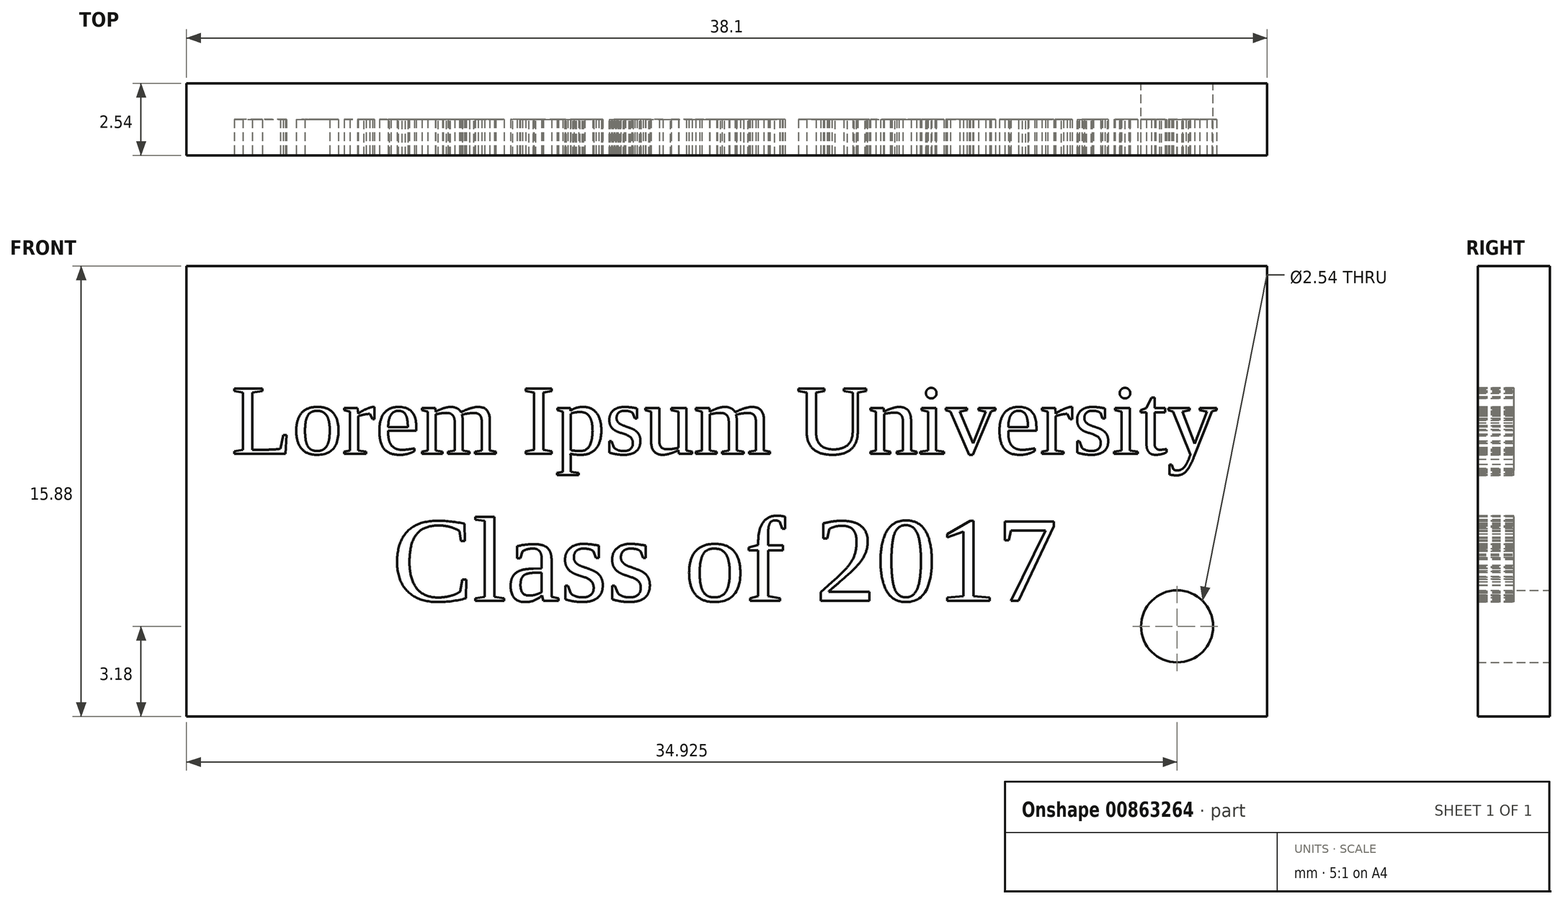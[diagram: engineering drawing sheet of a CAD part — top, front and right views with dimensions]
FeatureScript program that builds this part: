
annotation { "Feature Type Name" : "Feature", "Feature Type Description" : "" }
export const myFeature = defineFeature(function(context is Context, id is Id, definition is map)
    precondition{}
    {
        {
            var Q0;
            Q0=qCreatedBy(makeId("Front.planeOp"),FACE);
            var sketch = newSketch(context, id + "F0", { "sketchPlane" : qUnion([Q0])});
            skLineSegment(sketch, "E0.bottom", {"start": v(0, 0) * mm, "end": v(38.1, 0) * mm});
            skLineSegment(sketch, "E0.top", {"start": v(0, -15.88) * mm, "end": v(38.1, -15.88) * mm});
            skLineSegment(sketch, "E0.left", {"start": v(0, 0) * mm, "end": v(0, -15.88) * mm});
            skLineSegment(sketch, "E0.right", {"start": v(38.1, 0) * mm, "end": v(38.1, -15.88) * mm});
            skLineSegment(sketch, "E1.bottom", {"start": v(3.18, -3.18) * mm, "end": v(34.92, -3.18) * mm, "construction": true});
            skLineSegment(sketch, "E1.top", {"start": v(3.18, -12.7) * mm, "end": v(34.92, -12.7) * mm, "construction": true});
            skLineSegment(sketch, "E1.left", {"start": v(3.18, -3.18) * mm, "end": v(3.18, -12.7) * mm, "construction": true});
            skLineSegment(sketch, "E1.right", {"start": v(34.92, -3.18) * mm, "end": v(34.92, -12.7) * mm, "construction": true});
            skLineSegment(sketch, "E2.bottom", {"start": v(38.1, 0) * mm, "end": v(0, 0) * mm});
            skLineSegment(sketch, "E2.top", {"start": v(38.1, -15.87) * mm, "end": v(0, -15.87) * mm});
            skLineSegment(sketch, "E2.left", {"start": v(38.1, 0) * mm, "end": v(38.1, -15.87) * mm});
            skLineSegment(sketch, "E2.right", {"start": v(0, 0) * mm, "end": v(0, -15.87) * mm});
            skSolve(sketch);
        }
        {
            var Q0;
            Q0 = qSketchRegion(id + "F0", true);
            extrude(context, id + "F1", {"entities" : qUnion([Q0]), "depth" : 2.54 * mm, "offsetDistance" : 25.4 * mm});
        }
        {
            var Q0;
            Q0=makeQuery(id+"F1.opExtrude","CAP_FACE",FACE,{"disambiguationData":[OSD([sQuery(id+"F0.wireOp",EDGE,"E2.bottom"),sQuery(id+"F0.wireOp",EDGE,"E2.top"),sQuery(id+"F0.wireOp",EDGE,"E2.left"),sQuery(id+"F0.wireOp",EDGE,"E2.right")])],"isStart":false});
            var sketch = newSketch(context, id + "F2", { "sketchPlane" : qUnion([Q0])});
            skText(sketch, "E3", { "text": "Lorem Ipsum University ", "fontName": "Tinos-Regular.ttf"});
            skText(sketch, "E4", { "text": "Class of 2017", "fontName": "Tinos-Regular.ttf"});
            const initialGuessF2  = {"E3": [0.00159, -0.00662, 1, 0, 0.00253], "E4": [0.00725, -0.0118, 1, 0, 0.00307]};
            skSetInitialGuess(sketch, initialGuessF2);
            skSolve(sketch);
        }
        {
            var Q0;
            Q0 = qSketchRegion(id + "F2", true);
            extrude(context, id + "F3", {"entities" : qUnion([Q0]), "operationType" : NewBodyOperationType.REMOVE, "oppositeDirection" : true, "depth" : 1.27 * mm, "offsetDistance" : 25.4 * mm});
        }
        {
            var Q0;
            Q0=sQuery(id+"F0.wireOp",VERTEX,"E1.top.end");
            var Q1;
            Q1=makeQuery(id+"F1.opExtrude","SWEPT_BODY",BODY,{"disambiguationData":[OSD([sQuery(id+"F0.wireOp",EDGE,"E2.bottom"),sQuery(id+"F0.wireOp",EDGE,"E2.top"),sQuery(id+"F0.wireOp",EDGE,"E2.left"),sQuery(id+"F0.wireOp",EDGE,"E2.right")])]});
            hole(context, id + "F4", {"style" : HoleStyle.SIMPLE, "endStyle" : HoleEndStyle.THROUGH, "oppositeDirection" : true, "holeDiameter" : 2.54 * mm, "majorDiameter" : 6.35 * mm, "isTappedThrough" : true, "tappedDepth" : 12.7 * mm, "tapClearance" : 3, "locations" : qUnion([Q0]), "scope" : qUnion([Q1])});
        }
    });
